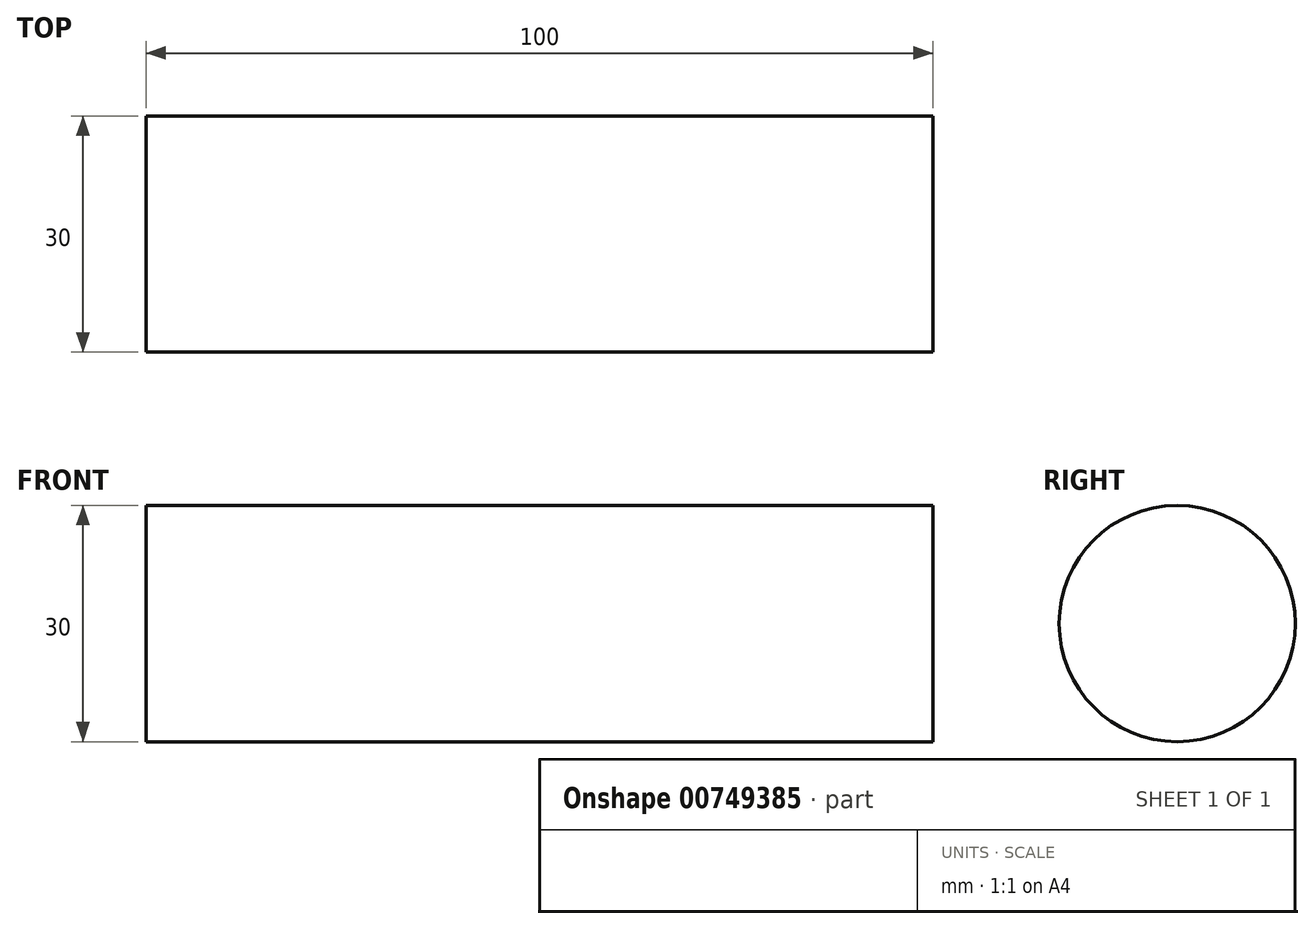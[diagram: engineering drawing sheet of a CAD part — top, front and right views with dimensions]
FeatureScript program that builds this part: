
annotation { "Feature Type Name" : "Feature", "Feature Type Description" : "" }
export const myFeature = defineFeature(function(context is Context, id is Id, definition is map)
    precondition{}
    {
        {
            var Q0;
            Q0=qCreatedBy(makeId("Front.planeOp"),FACE);
            var sketch = newSketch(context, id + "F0", { "sketchPlane" : qUnion([Q0])});
            skLineSegment(sketch, "E0.bottom", {"start": v(-50, 7.5) * mm, "end": v(50, 7.5) * mm});
            skLineSegment(sketch, "E0.top", {"start": v(-50, -7.5) * mm, "end": v(50, -7.5) * mm});
            skLineSegment(sketch, "E0.left", {"start": v(-50, 7.5) * mm, "end": v(-50, -7.5) * mm});
            skLineSegment(sketch, "E0.right", {"start": v(50, 7.5) * mm, "end": v(50, -7.5) * mm});
            skPoint(sketch, "E0.middle", {"position": v(0, 0) * mm});
            skSolve(sketch);
        }
        {
            var Q0;
            Q0=makeQuery(id+"F0.imprint","IMPRINT",FACE,{"disambiguationData":[TD([[makeQuery(id+"F0.imprint","IMPRINT",EDGE,{"derivedFrom":sQuery(id+"F0.wireOp",EDGE,"E0.bottom")}),-1.0]])]});
            var Q1;
            Q1=sQuery(id+"F0.wireOp",EDGE,"E0.top");
            revolve(context, id + "F1", {"surfaceOperationType" : NewSurfaceOperationType.NEW, "entities" : qUnion([Q0]), "axis" : qUnion([Q1]), "revolveType" : RevolveType.FULL});
        }
    });
